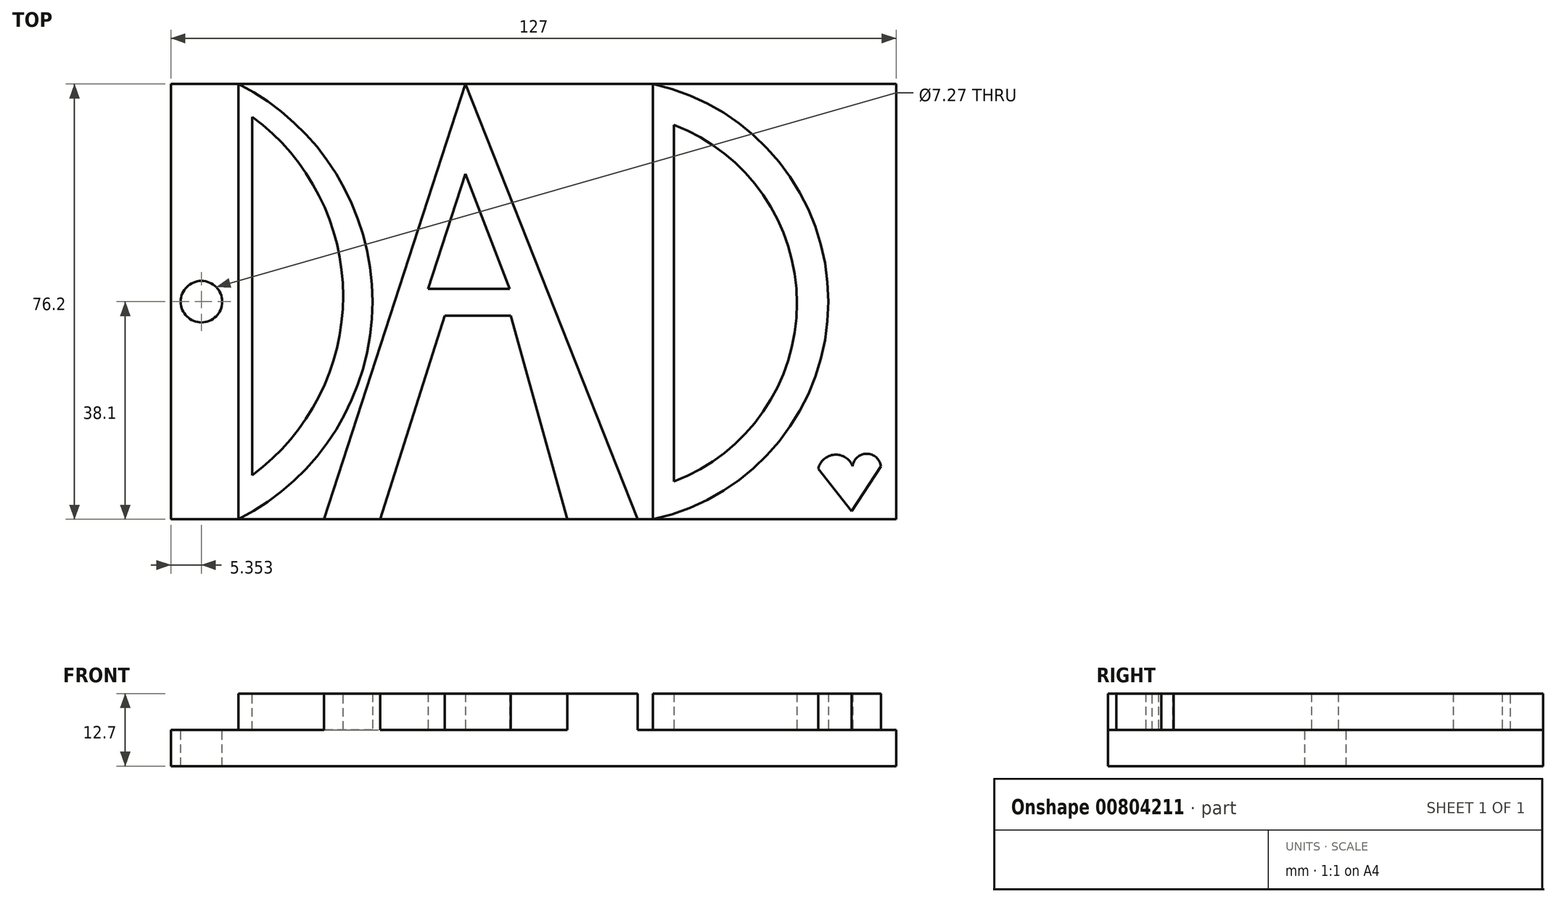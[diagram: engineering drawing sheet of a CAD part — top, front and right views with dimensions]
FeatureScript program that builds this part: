
annotation { "Feature Type Name" : "Feature", "Feature Type Description" : "" }
export const myFeature = defineFeature(function(context is Context, id is Id, definition is map)
    precondition{}
    {
        {
            var Q0;
            Q0=qCreatedBy(makeId("Top.planeOp"),FACE);
            var sketch = newSketch(context, id + "F0", { "sketchPlane" : qUnion([Q0])});
            skLineSegment(sketch, "E0", {"start": v(0, 0) * mm, "end": v(127, 0) * mm});
            skLineSegment(sketch, "E1", {"start": v(127, 0) * mm, "end": v(127, -76.2) * mm});
            skLineSegment(sketch, "E2", {"start": v(127, -76.2) * mm, "end": v(0, -76.2) * mm});
            skLineSegment(sketch, "E3", {"start": v(0, -76.2) * mm, "end": v(0, 0) * mm});
            skSolve(sketch);
        }
        {
            var Q0;
            Q0=makeQuery(id+"F0.imprint","IMPRINT",FACE,{"disambiguationData":[TD([[makeQuery(id+"F0.imprint","IMPRINT",EDGE,{"derivedFrom":sQuery(id+"F0.wireOp",EDGE,"E0")}),-1.0]])]});
            extrude(context, id + "F1", {"entities" : qUnion([Q0]), "depth" : 6.35 * mm, "offsetDistance" : 25.4 * mm});
        }
        {
            var Q0;
            Q0=makeQuery(id+"F1.opExtrude","CAP_FACE",FACE,{"disambiguationData":[OSD([sQuery(id+"F0.wireOp",EDGE,"E0"),sQuery(id+"F0.wireOp",EDGE,"E1"),sQuery(id+"F0.wireOp",EDGE,"E2"),sQuery(id+"F0.wireOp",EDGE,"E3")])],"isStart":false});
            var sketch = newSketch(context, id + "F2", { "sketchPlane" : qUnion([Q0])});
            skLineSegment(sketch, "E4", {"start": v(0, 0) * mm, "end": v(0, -38.1) * mm});
            skLineSegment(sketch, "E5", {"start": v(0, -38.1) * mm, "end": v(5.35, -38.1) * mm});
            skCircle(sketch, "E6", {"center": v(5.35, -38.1) * mm, "radius": 3.63 * mm});
            skSolve(sketch);
        }
        {
            var Q0;
            Q0=makeQuery(id+"F2.imprint","IMPRINT",FACE,{"disambiguationData":[TD([[makeQuery(id+"F2.imprint","IMPRINT",EDGE,{"derivedFrom":sQuery(id+"F2.wireOp",EDGE,"E6")}),1.0]])]});
            extrude(context, id + "F3", {"entities" : qUnion([Q0]), "operationType" : NewBodyOperationType.REMOVE, "endBound" : BoundingType.UP_TO_NEXT, "oppositeDirection" : true, "depth" : 25.4 * mm, "offsetDistance" : 25.4 * mm});
        }
        {
            var Q0;
            Q0=makeQuery(id+"F1.opExtrude","CAP_FACE",FACE,{"disambiguationData":[OSD([sQuery(id+"F0.wireOp",EDGE,"E0"),sQuery(id+"F0.wireOp",EDGE,"E1"),sQuery(id+"F0.wireOp",EDGE,"E2"),sQuery(id+"F0.wireOp",EDGE,"E3")])],"isStart":false});
            var sketch = newSketch(context, id + "F4", { "sketchPlane" : qUnion([Q0])});
            skLineSegment(sketch, "E7", {"start": v(0, 0) * mm, "end": v(11.84, 0) * mm});
            skLineSegment(sketch, "E8", {"start": v(11.84, 0) * mm, "end": v(11.84, -76.2) * mm});
            skArc(sketch, "E9", {"start": v(11.84, -76.2) * mm, "mid": v(35.29, -38.1) * mm, "end": v(11.84, 0) * mm});
            skSolve(sketch);
        }
        {
            var Q0;
            Q0=makeQuery(id+"F4.imprint","IMPRINT",FACE,{"disambiguationData":[TD([[makeQuery(id+"F4.imprint","IMPRINT",EDGE,{"derivedFrom":sQuery(id+"F4.wireOp",EDGE,"E8")}),1.0]])]});
            extrude(context, id + "F5", {"entities" : qUnion([Q0]), "operationType" : NewBodyOperationType.ADD, "depth" : 6.35 * mm, "offsetDistance" : 25.4 * mm});
        }
        {
            var Q0;
            Q0=makeQuery(id+"F5.opExtrude","CAP_FACE",FACE,{"disambiguationData":[OSD([sQuery(id+"F4.wireOp",EDGE,"E8"),sQuery(id+"F4.wireOp",EDGE,"E9")])],"isStart":false});
            var sketch = newSketch(context, id + "F6", { "sketchPlane" : qUnion([Q0])});
            skLineSegment(sketch, "E10", {"start": v(14.23, -5.75) * mm, "end": v(14.23, -68.48) * mm});
            skArc(sketch, "E11", {"start": v(14.23, -68.48) * mm, "mid": v(30.15, -37.11) * mm, "end": v(14.23, -5.75) * mm});
            skSolve(sketch);
        }
        {
            var Q0;
            Q0=makeQuery(id+"F6.imprint","IMPRINT",FACE,{"disambiguationData":[TD([[makeQuery(id+"F6.imprint","IMPRINT",EDGE,{"derivedFrom":sQuery(id+"F6.wireOp",EDGE,"E10")}),1.0]])]});
            extrude(context, id + "F7", {"entities" : qUnion([Q0]), "operationType" : NewBodyOperationType.REMOVE, "oppositeDirection" : true, "depth" : 6.35 * mm, "offsetDistance" : 25.4 * mm});
        }
        {
            var Q0;
            {var subQ0=sQuery(id+"F0.wireOp",EDGE,"E2");var subQ1=sQuery(id+"F0.wireOp",EDGE,"E1");var subQ2=sQuery(id+"F0.wireOp",EDGE,"E0");var subQ3=makeQuery(id+"F1.opExtrude","CAP_FACE",FACE,{"disambiguationData":[OSD([subQ2,subQ1,subQ0,sQuery(id+"F0.wireOp",EDGE,"E3")])],"isStart":false});Q0=makeQuery(id+"F5.boolean.opBoolean","SPLIT",FACE,{"disambiguationData":[TD([makeQuery(id+"F1.opExtrude","SWEPT_FACE",FACE,{"disambiguationData":[OSD([subQ1])]})])],"derivedFrom":subQ3});}
            var sketch = newSketch(context, id + "F8", { "sketchPlane" : qUnion([Q0])});
            skLineSegment(sketch, "E12", {"start": v(11.84, 0) * mm, "end": v(51.59, 0) * mm});
            skLineSegment(sketch, "E13", {"start": v(51.59, 0) * mm, "end": v(26.78, -76.2) * mm});
            skLineSegment(sketch, "E14", {"start": v(26.78, -76.2) * mm, "end": v(36.65, -76.2) * mm});
            skLineSegment(sketch, "E15", {"start": v(36.65, -76.2) * mm, "end": v(47.92, -40.57) * mm});
            skLineSegment(sketch, "E16", {"start": v(47.92, -40.57) * mm, "end": v(59.48, -40.57) * mm});
            skLineSegment(sketch, "E17", {"start": v(59.48, -40.57) * mm, "end": v(69.42, -76.2) * mm});
            skLineSegment(sketch, "E18", {"start": v(51.59, 0) * mm, "end": v(81.75, -76.2) * mm});
            skLineSegment(sketch, "E19", {"start": v(81.75, -76.2) * mm, "end": v(69.42, -76.2) * mm});
            skLineSegment(sketch, "E20", {"start": v(51.59, -15.76) * mm, "end": v(45.03, -35.89) * mm});
            skLineSegment(sketch, "E21", {"start": v(45.03, -35.89) * mm, "end": v(59.34, -35.89) * mm});
            skLineSegment(sketch, "E22", {"start": v(59.34, -35.89) * mm, "end": v(51.59, -15.76) * mm});
            skSolve(sketch);
        }
        {
            var Q0;
            Q0=makeQuery(id+"F8.imprint","IMPRINT",FACE,{"disambiguationData":[TD([[makeQuery(id+"F8.imprint","IMPRINT",EDGE,{"derivedFrom":sQuery(id+"F8.wireOp",EDGE,"E13")}),1.0]])]});
            extrude(context, id + "F9", {"entities" : qUnion([Q0]), "operationType" : NewBodyOperationType.ADD, "depth" : 6.35 * mm, "offsetDistance" : 25.4 * mm});
        }
        {
            var Q0;
            {var subQ0=sQuery(id+"F0.wireOp",EDGE,"E2");var subQ2=sQuery(id+"F0.wireOp",EDGE,"E1");var subQ3=makeQuery(id+"F1.opExtrude","SWEPT_FACE",FACE,{"disambiguationData":[OSD([subQ2])]});var subQ4=sQuery(id+"F0.wireOp",EDGE,"E0");var subQ5=makeQuery(id+"F1.opExtrude","CAP_FACE",FACE,{"disambiguationData":[OSD([subQ4,subQ2,subQ0,sQuery(id+"F0.wireOp",EDGE,"E3")])],"isStart":false});Q0=makeQuery(id+"F9.boolean.opBoolean","SPLIT",FACE,{"disambiguationData":[TD([subQ3])],"derivedFrom":makeQuery(id+"F5.boolean.opBoolean","SPLIT",FACE,{"disambiguationData":[TD([subQ3])],"derivedFrom":subQ5})});}
            var sketch = newSketch(context, id + "F10", { "sketchPlane" : qUnion([Q0])});
            skLineSegment(sketch, "E23", {"start": v(84.43, -76.2) * mm, "end": v(84.43, 0) * mm});
            skArc(sketch, "E24", {"start": v(84.43, -76.2) * mm, "mid": v(115.13, -38.1) * mm, "end": v(84.43, 0) * mm});
            skLineSegment(sketch, "E25", {"start": v(88.1, -7.16) * mm, "end": v(88.1, -69.6) * mm});
            skArc(sketch, "E26", {"start": v(88.1, -69.6) * mm, "mid": v(109.62, -38.38) * mm, "end": v(88.1, -7.16) * mm});
            skSolve(sketch);
        }
        {
            var Q0;
            Q0=makeQuery(id+"F10.imprint","IMPRINT",FACE,{"disambiguationData":[TD([[makeQuery(id+"F10.imprint","IMPRINT",EDGE,{"derivedFrom":sQuery(id+"F10.wireOp",EDGE,"E23")}),-1.0]])]});
            extrude(context, id + "F11", {"entities" : qUnion([Q0]), "operationType" : NewBodyOperationType.ADD, "depth" : 6.35 * mm, "offsetDistance" : 25.4 * mm});
        }
        {
            var Q0;
            {var subQ0=sQuery(id+"F0.wireOp",EDGE,"E2");var subQ2=sQuery(id+"F0.wireOp",EDGE,"E1");var subQ3=makeQuery(id+"F1.opExtrude","SWEPT_FACE",FACE,{"disambiguationData":[OSD([subQ2])]});var subQ4=sQuery(id+"F0.wireOp",EDGE,"E0");var subQ5=makeQuery(id+"F1.opExtrude","CAP_FACE",FACE,{"disambiguationData":[OSD([subQ4,subQ2,subQ0,sQuery(id+"F0.wireOp",EDGE,"E3")])],"isStart":false});Q0=makeQuery(id+"F11.boolean.opBoolean","SPLIT",FACE,{"disambiguationData":[TD([subQ3])],"derivedFrom":makeQuery(id+"F9.boolean.opBoolean","SPLIT",FACE,{"disambiguationData":[TD([subQ3])],"derivedFrom":makeQuery(id+"F5.boolean.opBoolean","SPLIT",FACE,{"disambiguationData":[TD([subQ3])],"derivedFrom":subQ5})})});}
            var sketch = newSketch(context, id + "F12", { "sketchPlane" : qUnion([Q0])});
            skLineSegment(sketch, "E27", {"start": v(113.35, -67.36) * mm, "end": v(119.22, -74.77) * mm});
            skLineSegment(sketch, "E28", {"start": v(119.22, -74.77) * mm, "end": v(124.32, -66.9) * mm});
            skArc(sketch, "E29", {"start": v(124.32, -66.9) * mm, "mid": v(121.85, -64.72) * mm, "end": v(119.38, -66.9) * mm});
            skArc(sketch, "E30", {"start": v(119.38, -66.9) * mm, "mid": v(116.2, -64.89) * mm, "end": v(113.35, -67.36) * mm});
            skSolve(sketch);
        }
        {
            var Q0;
            Q0=makeQuery(id+"F12.imprint","IMPRINT",FACE,{"disambiguationData":[TD([[makeQuery(id+"F12.imprint","IMPRINT",EDGE,{"derivedFrom":sQuery(id+"F12.wireOp",EDGE,"E27")}),1.0]])]});
            extrude(context, id + "F13", {"entities" : qUnion([Q0]), "operationType" : NewBodyOperationType.ADD, "depth" : 6.35 * mm, "offsetDistance" : 25.4 * mm});
        }
    });
